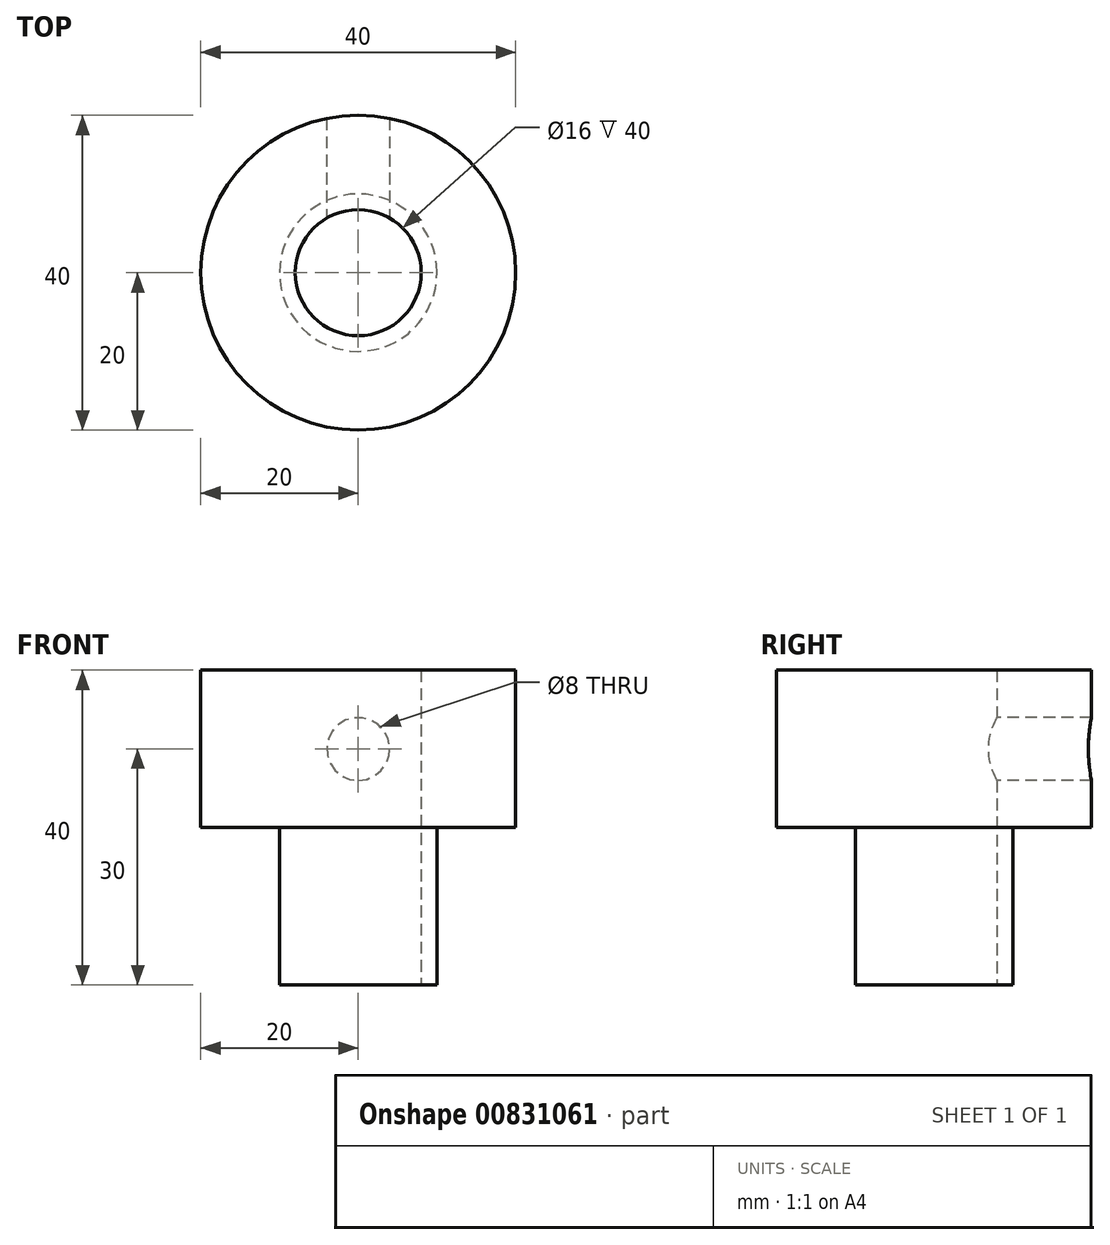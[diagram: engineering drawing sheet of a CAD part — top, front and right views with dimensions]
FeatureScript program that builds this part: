
annotation { "Feature Type Name" : "Feature", "Feature Type Description" : "" }
export const myFeature = defineFeature(function(context is Context, id is Id, definition is map)
    precondition{}
    {
        {
            var Q0;
            Q0=qCreatedBy(makeId("Top.planeOp"),FACE);
            var sketch = newSketch(context, id + "F0", { "sketchPlane" : qUnion([Q0])});
            skCircle(sketch, "E0", {"center": v(0, 0) * mm, "radius": 20 * mm});
            skCircle(sketch, "E1", {"center": v(0, 0) * mm, "radius": 8 * mm});
            skSolve(sketch);
        }
        {
            var Q0;
            Q0=makeQuery(id+"F0.imprint","IMPRINT",FACE,{"disambiguationData":[TD([[makeQuery(id+"F0.imprint","IMPRINT",EDGE,{"derivedFrom":sQuery(id+"F0.wireOp",EDGE,"E0")}),1.0]])]});
            extrude(context, id + "F1", {"entities" : qUnion([Q0]), "depth" : 20 * mm, "offsetDistance" : 25 * mm});
        }
        {
            var Q0;
            Q0=makeQuery(id+"F1.opExtrude","CAP_FACE",FACE,{"disambiguationData":[OSD([sQuery(id+"F0.wireOp",EDGE,"E0"),sQuery(id+"F0.wireOp",EDGE,"E1")])],"isStart":true});
            var sketch = newSketch(context, id + "F2", { "sketchPlane" : qUnion([Q0])});
            skCircle(sketch, "E2", {"center": v(0, 0) * mm, "radius": 10 * mm});
            skCircle(sketch, "E3", {"center": v(0, 0) * mm, "radius": 8 * mm});
            skSolve(sketch);
        }
        {
            var Q0;
            Q0=makeQuery(id+"F2.imprint","IMPRINT",FACE,{"disambiguationData":[TD([[makeQuery(id+"F2.imprint","IMPRINT",EDGE,{"derivedFrom":sQuery(id+"F2.wireOp",EDGE,"E2")}),1.0]])]});
            extrude(context, id + "F3", {"entities" : qUnion([Q0]), "operationType" : NewBodyOperationType.ADD, "depth" : 20 * mm, "offsetDistance" : 25 * mm});
        }
        {
            var Q0;
            Q0=qCreatedBy(makeId("Front.planeOp"),FACE);
            var sketch = newSketch(context, id + "F4", { "sketchPlane" : qUnion([Q0])});
            skCircle(sketch, "E4", {"center": v(0, 10) * mm, "radius": 4 * mm});
            skSolve(sketch);
        }
        {
            var Q0;
            Q0=makeQuery(id+"F4.imprint","IMPRINT",FACE,{"disambiguationData":[TD([[makeQuery(id+"F4.imprint","IMPRINT",EDGE,{"derivedFrom":sQuery(id+"F4.wireOp",EDGE,"E4")}),1.0]])]});
            extrude(context, id + "F5", {"entities" : qUnion([Q0]), "operationType" : NewBodyOperationType.REMOVE, "oppositeDirection" : true, "depth" : 25 * mm, "offsetDistance" : 25 * mm});
        }
    });
